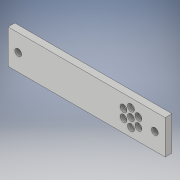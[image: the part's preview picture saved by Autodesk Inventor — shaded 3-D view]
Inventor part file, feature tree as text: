
AUTODESK INVENTOR PART (.ipt)
format: ipt  version: 2019 (Build 230136000, 136)  size: 139,776 bytes
history: native  units: in
note: dims shown in document units (in); Inventor stores cm internally (conversion verified against a paired STEP export)
features: sketch x3, hole x3, extrude x1, projected_geometry x1
ambient origin geometry x8: Origin, YZ Plane, XZ Plane, XY Plane, X Axis, Y Axis, Z Axis, Center Point
bodies: Solid1 (feature_tree)
feature tree (8):
  extrude  "Extrusion1"  Depth=1.25in
  sketch  "Sketch2"  dims[d2=0.25in d3=0.0in d7=90.0deg]
  hole  "Hole2"  [1 undecoded]
  hole  "Hole3"  [1 undecoded]
  hole  "Hole4"  [1 undecoded]
  sketch  "Sketch1"  dims[d0=5.75in d1=1.25in]
  sketch  "Sketch5"  dims[d9=0.63in d17=1.25in d46=2.3622in d48=360.0deg d50=0.134in d51=0.25in d52=0.256in d53=0.134in d54=0.5635in d55=0.3in d56=0.8108in d57=0.25in d58=0.25in d59=0.256in d60=0.134in d61=0.5635in d62=0.3in d63=0.8108in d64=1.25in d65=0.625in d68=0.625in d69=0.375in d71=0.375in d72=0.25in d73=0.25in d74=0.256in d75=0.134in d76=0.5635in d77=0.3in d78=0.8108in d79=1.25in d80=0.625in d81=0.625in]
  projected_geometry  "Projected Loop1"
note: 3 required parameter values undecoded (feature->parameter linkage not recoverable at this tier; creation-order binding heuristic only, values carry confidence <= 0.55)
